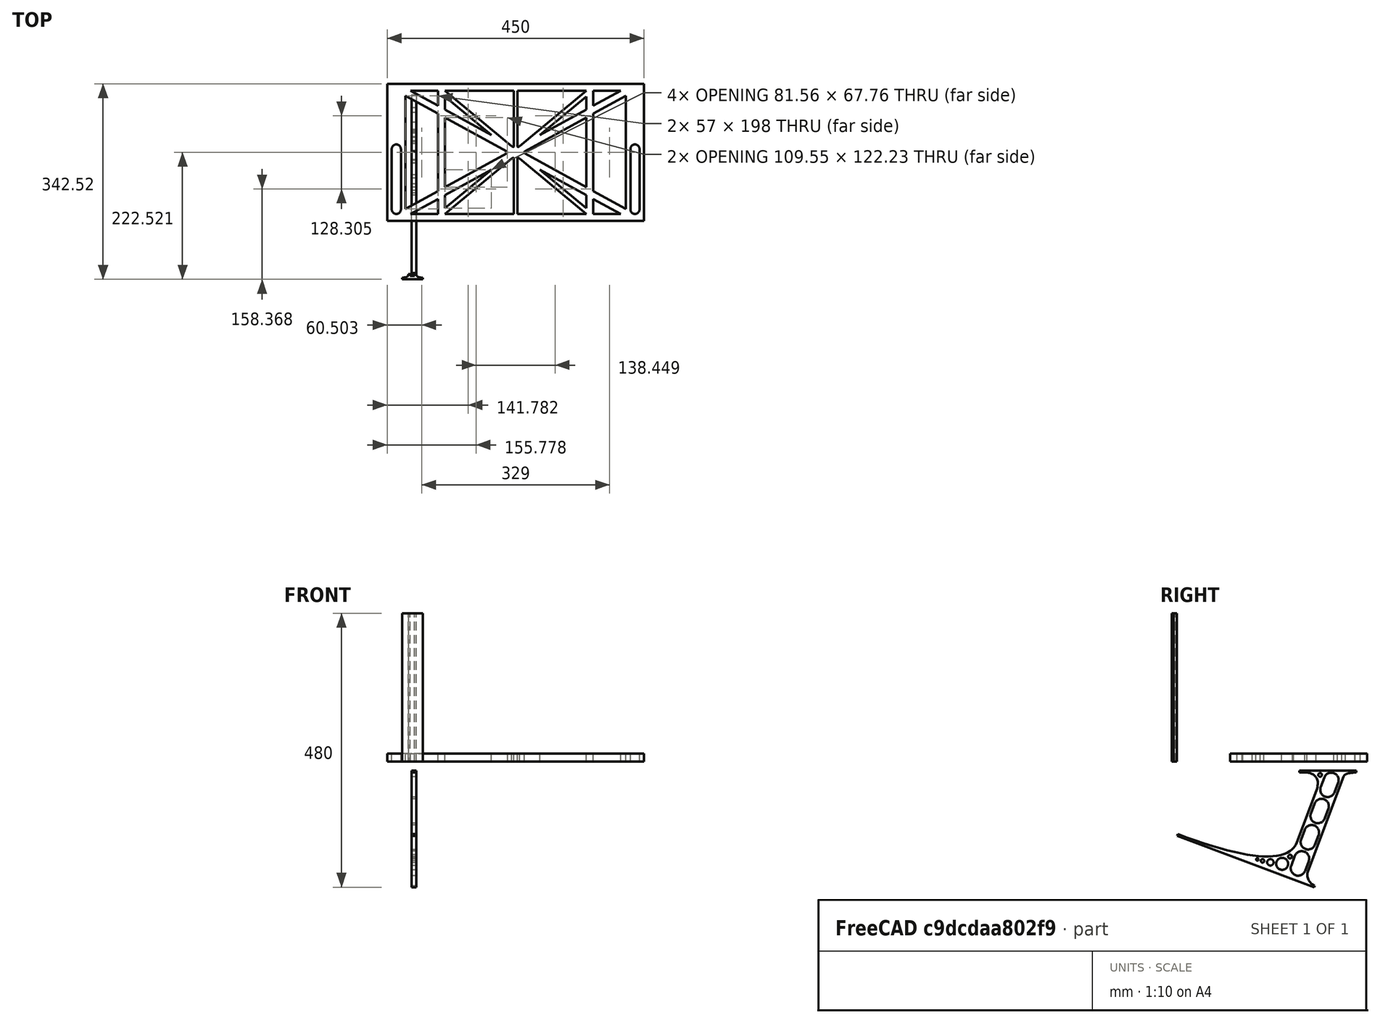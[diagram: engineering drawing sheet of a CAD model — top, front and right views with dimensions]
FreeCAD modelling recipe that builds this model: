
FCSTD DOCUMENT  (FreeCAD 0.19R0.19.2)
Label: laptopStand059
License: All rights reserved
LicenseURL: http://en.wikipedia.org/wiki/All_rights_reserved
objects: Sketcher::SketchObject×3, Part::Extrusion×3
note: 6 computed .brp shape members not serialized (recipe doc carries the construction recipe); baked Part::Feature solids carry a one-line shape summary decoded from their .brp

FEATURE [Sketcher::SketchObject] Sketch
  FullyConstrained = false
  sketch-geometry (100):
    g0: LineSegment StartX=375.073 StartY=115.221 StartZ=0 EndX=318.073 EndY=83.9235 EndZ=0
    g1: LineSegment StartX=-10.9272 StartY=-82.7794 StartZ=0 EndX=46.0728 EndY=-51.4823 EndZ=0
    g2: LineSegment StartX=-1.92718 StartY=124.221 StartZ=0 EndX=46.0728 EndY=97.8651 EndZ=0
    g3: LineSegment StartX=366.073 StartY=-91.7794 StartZ=0 EndX=318.073 EndY=-65.424 EndZ=0
    g4: LineSegment StartX=-10.9272 StartY=115.221 StartZ=0 EndX=-10.9272 EndY=-82.7794 EndZ=0
    g5: LineSegment StartX=375.073 StartY=-82.7794 StartZ=0 EndX=375.073 EndY=115.221 EndZ=0
    g6: LineSegment StartX=-1.92719 StartY=-91.7794 StartZ=0 EndX=46.0728 EndY=-91.7794 EndZ=0
    g7: LineSegment StartX=318.073 StartY=124.221 StartZ=0 EndX=366.073 EndY=124.221 EndZ=0
    g8: LineSegment StartX=306.073 StartY=-81.8102 StartZ=0 EndX=224.513 EndY=-14.0532 EndZ=0
    g9: LineSegment StartX=58.0728 StartY=114.251 StartZ=0 EndX=139.632 EndY=46.4944 EndZ=0
    g10: LineSegment StartX=306.073 StartY=124.221 StartZ=0 EndX=189.124 EndY=27.0628 EndZ=0
    g11: LineSegment StartX=58.0728 StartY=-91.7794 StartZ=0 EndX=175.022 EndY=5.37834 EndZ=0
    g12: LineSegment StartX=46.0728 StartY=124.221 StartZ=0 EndX=46.0728 EndY=97.8651 EndZ=0
    g13: LineSegment StartX=58.0728 StartY=-81.8102 StartZ=0 EndX=58.0728 EndY=-58.8351 EndZ=0
    g14: LineSegment StartX=318.073 StartY=124.221 StartZ=0 EndX=318.073 EndY=97.8651 EndZ=0
    g15: LineSegment StartX=306.073 StartY=114.251 StartZ=0 EndX=306.073 EndY=91.2763 EndZ=0
    g16: LineSegment StartX=224.513 StartY=46.4944 StartZ=0 EndX=306.073 EndY=114.251 EndZ=0
    g17: LineSegment StartX=175.022 StartY=27.0628 StartZ=0 EndX=58.0728 EndY=124.221 EndZ=0
    g18: LineSegment StartX=139.632 StartY=-14.0532 StartZ=0 EndX=58.0728 EndY=-81.8102 EndZ=0
    g19: LineSegment StartX=224.513 StartY=46.4944 StartZ=0 EndX=306.073 EndY=91.2763 EndZ=0
    g20: LineSegment StartX=139.632 StartY=-14.0532 StartZ=0 EndX=58.0728 EndY=-58.8351 EndZ=0
    g21: LineSegment StartX=189.124 StartY=5.37834 StartZ=0 EndX=306.073 EndY=-91.7794 EndZ=0
    g22: LineSegment StartX=306.073 StartY=77.3346 StartZ=0 EndX=306.073 EndY=-44.8935 EndZ=0
    g23: LineSegment StartX=318.073 StartY=83.9235 StartZ=0 EndX=318.073 EndY=-51.4823 EndZ=0
    g24: LineSegment StartX=318.073 StartY=97.8651 StartZ=0 EndX=366.073 EndY=124.221 EndZ=0
    g25: LineSegment StartX=306.073 StartY=-58.8351 StartZ=0 EndX=224.513 EndY=-14.0532 EndZ=0
    g26: LineSegment StartX=306.073 StartY=-58.8351 StartZ=0 EndX=306.073 EndY=-81.8102 EndZ=0
    g27: LineSegment StartX=318.073 StartY=-51.4823 StartZ=0 EndX=375.073 EndY=-82.7794 EndZ=0
    g28: LineSegment StartX=318.073 StartY=-65.424 StartZ=0 EndX=318.073 EndY=-91.7794 EndZ=0
    g29: LineSegment StartX=318.073 StartY=-91.7794 StartZ=0 EndX=366.073 EndY=-91.7794 EndZ=0
    g30: LineSegment StartX=58.0728 StartY=-44.8935 StartZ=0 EndX=58.0728 EndY=77.3346 EndZ=0
    g31: LineSegment StartX=46.0728 StartY=-65.424 StartZ=0 EndX=-1.92719 EndY=-91.7794 EndZ=0
    g32: LineSegment StartX=46.0728 StartY=-65.424 StartZ=0 EndX=46.0728 EndY=-91.7794 EndZ=0
    g33: LineSegment StartX=58.0728 StartY=91.2763 StartZ=0 EndX=58.0728 EndY=114.251 EndZ=0
    g34: LineSegment StartX=46.0728 StartY=83.9235 StartZ=0 EndX=46.0728 EndY=-51.4823 EndZ=0
    g35: LineSegment StartX=46.0728 StartY=124.221 StartZ=0 EndX=-1.92719 EndY=124.221 EndZ=0
    g36: LineSegment StartX=58.0728 StartY=91.2763 StartZ=0 EndX=139.632 EndY=46.4944 EndZ=0
    g37: LineSegment StartX=46.0728 StartY=83.9235 StartZ=0 EndX=-10.9272 EndY=115.221 EndZ=0
    g38: LineSegment StartX=-42.9272 StartY=136.221 StartZ=0 EndX=-42.9272 EndY=-103.779 EndZ=0
    g39: LineSegment StartX=407.073 StartY=136.221 StartZ=0 EndX=407.073 EndY=-103.779 EndZ=0
    g40: LineSegment StartX=179.022 StartY=27.0628 StartZ=0 EndX=179.022 EndY=124.221 EndZ=0
    g41: LineSegment StartX=185.124 StartY=27.0628 StartZ=0 EndX=185.124 EndY=124.221 EndZ=0
    g42: ArcOfCircle CenterX=-26.9272 CenterY=22.1087 CenterZ=0 NormalX=0 NormalY=0 NormalZ=1 AngleXU=0 Radius=8 StartAngle=1e-16 EndAngle=3.14159
    g43: ArcOfCircle CenterX=-26.9272 CenterY=-83.7794 CenterZ=0 NormalX=0 NormalY=0 NormalZ=1 AngleXU=0 Radius=8 StartAngle=3.14159 EndAngle=6.28319
    g44: LineSegment StartX=-34.9272 StartY=22.1087 StartZ=0 EndX=-34.9272 EndY=-83.7794 EndZ=0
    g45: LineSegment StartX=-18.9272 StartY=22.1087 StartZ=0 EndX=-18.9272 EndY=-83.7794 EndZ=0
    g46: LineSegment StartX=185.124 StartY=-91.7794 StartZ=0 EndX=306.073 EndY=-91.7794 EndZ=0
    g47: LineSegment StartX=179.022 StartY=-91.7794 StartZ=0 EndX=58.0728 EndY=-91.7794 EndZ=0
    g48: LineSegment StartX=306.073 StartY=124.221 StartZ=0 EndX=185.124 EndY=124.221 EndZ=0
    g49: LineSegment StartX=179.022 StartY=124.221 StartZ=0 EndX=58.0728 EndY=124.221 EndZ=0
    g50: ArcOfCircle CenterX=391.073 CenterY=22.1087 CenterZ=0 NormalX=0 NormalY=0 NormalZ=1 AngleXU=0 Radius=8 StartAngle=-4.4e-15 EndAngle=3.14159
    g51: LineSegment StartX=399.073 StartY=22.1087 StartZ=0 EndX=399.073 EndY=-83.7794 EndZ=0
    g52: LineSegment StartX=383.073 StartY=22.1087 StartZ=0 EndX=383.073 EndY=-83.7794 EndZ=0
    g53: ArcOfCircle CenterX=391.073 CenterY=-83.7794 CenterZ=0 NormalX=0 NormalY=0 NormalZ=1 AngleXU=0 Radius=8 StartAngle=3.14159 EndAngle=6.28319
    g54: Circle CenterX=175.022 CenterY=27.0628 CenterZ=0 NormalX=0 NormalY=0 NormalZ=1 AngleXU=0 Radius=1
    g55: Circle CenterX=179.022 CenterY=24.8665 CenterZ=0 NormalX=0 NormalY=0 NormalZ=1 AngleXU=0 Radius=1
    g56: Circle CenterX=179.022 CenterY=27.0628 CenterZ=0 NormalX=0 NormalY=0 NormalZ=1 AngleXU=0 Radius=1
    g57: BSplineCurve PolesCount=3 KnotsCount=2 Degree=2 IsPeriodic=0
    g58: GeomPoint X=175.022 Y=27.0628 Z=0
    g59: GeomPoint X=179.022 Y=27.0628 Z=0
    g60: Circle CenterX=189.124 CenterY=27.0628 CenterZ=0 NormalX=0 NormalY=0 NormalZ=1 AngleXU=0 Radius=1
    g61: Circle CenterX=185.124 CenterY=24.8665 CenterZ=0 NormalX=0 NormalY=0 NormalZ=1 AngleXU=0 Radius=1
    g62: Circle CenterX=185.124 CenterY=27.0628 CenterZ=0 NormalX=0 NormalY=0 NormalZ=1 AngleXU=0 Radius=1
    g63: BSplineCurve PolesCount=3 KnotsCount=2 Degree=2 IsPeriodic=0
    g64: GeomPoint X=189.124 Y=27.0628 Z=0
    g65: GeomPoint X=185.124 Y=27.0628 Z=0
    g66: Circle CenterX=175.022 CenterY=5.37834 CenterZ=0 NormalX=0 NormalY=0 NormalZ=1 AngleXU=0 Radius=1
    g67: Circle CenterX=179.022 CenterY=7.57463 CenterZ=0 NormalX=0 NormalY=0 NormalZ=1 AngleXU=0 Radius=1
    g68: Circle CenterX=179.022 CenterY=5.34704 CenterZ=0 NormalX=0 NormalY=0 NormalZ=1 AngleXU=0 Radius=1
    g69: BSplineCurve PolesCount=3 KnotsCount=2 Degree=2 IsPeriodic=0
    g70: GeomPoint X=175.022 Y=5.37834 Z=0
    g71: GeomPoint X=179.022 Y=5.34704 Z=0
    g72: Circle CenterX=189.124 CenterY=5.37834 CenterZ=0 NormalX=0 NormalY=0 NormalZ=1 AngleXU=0 Radius=1
    g73: Circle CenterX=185.124 CenterY=7.57463 CenterZ=0 NormalX=0 NormalY=0 NormalZ=1 AngleXU=0 Radius=1
    g74: Circle CenterX=185.124 CenterY=5.34704 CenterZ=0 NormalX=0 NormalY=0 NormalZ=1 AngleXU=0 Radius=1
    g75: BSplineCurve PolesCount=3 KnotsCount=2 Degree=2 IsPeriodic=0
    g76: GeomPoint X=189.124 Y=5.37834 Z=0
    g77: GeomPoint X=185.124 Y=5.34704 Z=0
    g78: LineSegment StartX=179.022 StartY=5.34704 StartZ=0 EndX=179.022 EndY=-91.7794 EndZ=0
    g79: LineSegment StartX=185.124 StartY=-91.7794 StartZ=0 EndX=185.124 EndY=5.34704 EndZ=0
    g80: Circle CenterX=165.871 CenterY=18.1458 CenterZ=0 NormalX=0 NormalY=0 NormalZ=1 AngleXU=0 Radius=1
    g81: Circle CenterX=169.377 CenterY=16.2206 CenterZ=0 NormalX=0 NormalY=0 NormalZ=1 AngleXU=0 Radius=1
    g82: Circle CenterX=165.871 CenterY=14.2954 CenterZ=0 NormalX=0 NormalY=0 NormalZ=1 AngleXU=0 Radius=1
    g83: BSplineCurve PolesCount=3 KnotsCount=2 Degree=2 IsPeriodic=0
    g84: GeomPoint X=165.871 Y=18.1458 Z=0
    g85: GeomPoint X=165.871 Y=14.2954 Z=0
    g86: Circle CenterX=198.275 CenterY=18.1458 CenterZ=0 NormalX=0 NormalY=0 NormalZ=1 AngleXU=0 Radius=1
    g87: Circle CenterX=194.768 CenterY=16.2206 CenterZ=0 NormalX=0 NormalY=0 NormalZ=1 AngleXU=0 Radius=1
    g88: Circle CenterX=198.275 CenterY=14.2954 CenterZ=0 NormalX=0 NormalY=0 NormalZ=1 AngleXU=0 Radius=1
    g89: BSplineCurve PolesCount=3 KnotsCount=2 Degree=2 IsPeriodic=0
    g90: GeomPoint X=198.275 Y=18.1458 Z=0
    g91: GeomPoint X=198.275 Y=14.2954 Z=0
    g92: LineSegment StartX=165.871 StartY=18.1458 StartZ=0 EndX=58.0728 EndY=77.3346 EndZ=0
    g93: LineSegment StartX=58.0728 StartY=-44.8935 StartZ=0 EndX=165.871 EndY=14.2954 EndZ=0
    g94: LineSegment StartX=198.275 StartY=18.1458 StartZ=0 EndX=306.073 EndY=77.3346 EndZ=0
    g95: LineSegment StartX=198.275 StartY=14.2954 StartZ=0 EndX=306.073 EndY=-44.8935 EndZ=0
    g96: LineSegment StartX=407.073 StartY=-103.779 StartZ=0 EndX=-42.9272 EndY=-103.779 EndZ=0
    g97: LineSegment StartX=407.073 StartY=136.221 StartZ=0 EndX=-42.9272 EndY=136.221 EndZ=0
    g98: LineSegment StartX=-10.9272 StartY=115.221 StartZ=0 EndX=-10.9272 EndY=140.791 EndZ=0
    g99: LineSegment StartX=-10.9272 StartY=140.791 StartZ=0 EndX=-26.9272 EndY=140.791 EndZ=0
  constraints (181):
    c: Horizontal(g6)
    c: Horizontal(g7)
    c: Coincident(g36,g9)
    c: Coincident(g16,g19)
    c: Coincident(g20,g18)
    c: Coincident(g25,g8)
    c: Coincident(g16,g15)
    c: Tangent(g15,g22)
    c: Tangent(g14,g23)
    c: Coincident(g19,g15)
    c: Tangent(g19,g24)
    c: Coincident(g0,g23)
    c: Coincident(g26,g8)
    c: Tangent(g3,g25)
    c: Tangent(g22,g26)
    c: Coincident(g23,g27)
    c: Coincident(g28,g3)
    c: Tangent(g23,g28)
    c: Coincident(g18,g13)
    c: Tangent(g13,g30)
    c: Coincident(g20,g13)
    c: Tangent(g20,g31)
    c: Coincident(g32,g31)
    c: Tangent(g12,g32)
    c: Coincident(g1,g34)
    c: Tangent(g30,g33)
    c: Tangent(g12,g34)
    c: Coincident(g9,g33)
    c: Coincident(g2,g12)
    c: Coincident(g36,g33)
    c: Tangent(g2,g36)
    c: Coincident(g37,g34)
    c: Block(g17)
    c: Block(g10)
    c: Block(g14)
    c: Block(g24)
    c: Block(g0)
    c: Block(g27)
    c: Block(g5)
    c: Block(g25)
    c: Block(g26)
    c: Block(g3)
    c: Block(g28)
    c: Block(g16)
    c: Block(g21)
    c: Block(g11)
    c: Block(g20)
    c: Block(g18)
    c: Block(g32)
    c: Block(g31)
    c: Block(g1)
    c: Block(g4)
    c: Block(g37)
    c: Block(g2)
    c: Block(g12)
    c: Block(g9)
    c: Block(g33)
    c: Block(g22)
    c: Block(g35)
    c: Block(g7)
    c: Block(g29)
    c: Block(g6)
    c: Vertical(g38)
    c: Vertical(g39)
    c: Block(g39)
    c: Block(g38)
    c: Vertical(g40)
    c: Vertical(g41)
    c: Block(g40)
    c: Block(g41)
    c: Tangent(g42,g45) = 1.5708
    c: Tangent(g42,g44) = -1.5708
    c: Tangent(g44,g43) = -1.5708
    c: Tangent(g45,g43) = 1.5708
    c: Vertical(g44)
    c: Equal(g42,g43)
    c: Block(g45)
    c: Block(g44)
    c: Coincident(g46,g21)
    c: Horizontal(g46)
    c: Coincident(g47,g11)
    c: Horizontal(g47)
    c: Coincident(g48,g10)
    c: Coincident(g48,g41)
    c: Horizontal(g48)
    c: Coincident(g49,g40)
    c: Coincident(g49,g17)
    c: Horizontal(g49)
    c: Tangent(g50,g51) = 1.5708
    c: Tangent(g51,g53) = 1.5708
    c: Equal(g50,g53)
    c: Coincident(g52,g50)
    c: Coincident(g52,g53)
    c: Block(g51)
    c: Block(g52)
    c: Coincident(g57,g17)
    c: Weight(g54) = 1
    c: Equal(g54,g55)
    c: Equal(g54,g56)
    c: Coincident(g57,g40)
    c: InternalAlignment(g54,g57)
    c: InternalAlignment(g55,g57)
    c: InternalAlignment(g56,g57)
    c: InternalAlignment(g58,g57)
    c: InternalAlignment(g59,g57)
    c: Coincident(g63,g10)
    c: Weight(g60) = 1
    c: Equal(g60,g61)
    c: Equal(g60,g62)
    c: Coincident(g63,g41)
    c: InternalAlignment(g60,g63)
    c: InternalAlignment(g61,g63)
    c: InternalAlignment(g62,g63)
    c: InternalAlignment(g64,g63)
    c: InternalAlignment(g65,g63)
    c: Block(g63)
    c: Block(g57)
    c: Coincident(g69,g11)
    c: Weight(g66) = 1
    c: Equal(g66,g67)
    c: Equal(g66,g68)
    c: InternalAlignment(g66,g69)
    c: InternalAlignment(g67,g69)
    c: InternalAlignment(g68,g69)
    c: InternalAlignment(g70,g69)
    c: InternalAlignment(g71,g69)
    c: Weight(g72) = 1
    c: Equal(g72,g73)
    c: Equal(g72,g74)
    c: InternalAlignment(g72,g75)
    c: InternalAlignment(g73,g75)
    c: InternalAlignment(g74,g75)
    c: InternalAlignment(g76,g75)
    c: InternalAlignment(g77,g75)
    c: Block(g75)
    c: Block(g69)
    c: Coincident(g78,g69)
    c: Coincident(g78,g47)
    c: Vertical(g78)
    c: Coincident(g79,g46)
    c: Coincident(g79,g75)
    c: Vertical(g79)
    c: Weight(g80) = 1
    c: Equal(g80,g81)
    c: Equal(g80,g82)
    c: InternalAlignment(g80,g83)
    c: InternalAlignment(g81,g83)
    c: InternalAlignment(g82,g83)
    c: InternalAlignment(g84,g83)
    c: InternalAlignment(g85,g83)
    c: Weight(g86) = 1
    c: Equal(g86,g87)
    c: Equal(g86,g88)
    c: InternalAlignment(g86,g89)
    c: InternalAlignment(g87,g89)
    c: InternalAlignment(g88,g89)
    c: InternalAlignment(g90,g89)
    c: InternalAlignment(g91,g89)
    c: Block(g83)
    c: Block(g89)
    c: Coincident(g92,g83)
    c: Coincident(g92,g30)
    c: Coincident(g93,g30)
    c: Coincident(g93,g83)
    c: Coincident(g94,g89)
    c: Coincident(g94,g22)
    c: Coincident(g95,g89)
    c: Coincident(g95,g22)
    c: Block(g30)
    c: Coincident(g96,g39)
    c: Coincident(g96,g38)
    c: Horizontal(g96)
    c: Distance(g96) = 450
    c: Coincident(g97,g39)
    c: Coincident(g97,g38)
    c: Horizontal(g97)
    c: Coincident(g98,g4)
    c: Vertical(g98)
    c: Coincident(g99,g98)
    c: Horizontal(g99)
    c: Distance(g99) = 16
FEATURE [Sketcher::SketchObject] Sketch001
  FullyConstrained = true
  MapMode = 4
  Placement = pos=(0,0,0) rot=(0.57735,0.57735,0.57735;2.0944rad)
  Support = -> [Sketch]
  sketch-geometry (46):
    g0: BSplineCurve PolesCount=3 KnotsCount=2 Degree=2 IsPeriodic=0
    g1: ArcOfCircle CenterX=73.1223 CenterY=-32.291 CenterZ=0 NormalX=0 NormalY=0 NormalZ=1 AngleXU=0 Radius=13 StartAngle=5.92268 EndAngle=9.06428
    g2: ArcOfCircle CenterX=66.7816 CenterY=-49.1439 CenterZ=0 NormalX=0 NormalY=0 NormalZ=1 AngleXU=0 Radius=13 StartAngle=2.78068 EndAngle=5.92131
    g3: ArcOfCircle CenterX=55.9263 CenterY=-78.1807 CenterZ=0 NormalX=0 NormalY=0 NormalZ=1 AngleXU=0 Radius=13 StartAngle=5.92268 EndAngle=9.06428
    g4: ArcOfCircle CenterX=49.5884 CenterY=-95.0342 CenterZ=0 NormalX=0 NormalY=0 NormalZ=1 AngleXU=0 Radius=13 StartAngle=2.78068 EndAngle=5.92131
    g5: ArcOfCircle CenterX=38.7206 CenterY=-124.067 CenterZ=0 NormalX=0 NormalY=0 NormalZ=1 AngleXU=0 Radius=13 StartAngle=5.92268 EndAngle=9.06428
    g6: ArcOfCircle CenterX=32.3875 CenterY=-140.92 CenterZ=0 NormalX=0 NormalY=0 NormalZ=1 AngleXU=0 Radius=13 StartAngle=2.78068 EndAngle=5.92131
    g7: ArcOfCircle CenterX=21.4715 CenterY=-169.934 CenterZ=0 NormalX=0 NormalY=0 NormalZ=1 AngleXU=0 Radius=13 StartAngle=5.92268 EndAngle=9.06428
    g8: ArcOfCircle CenterX=15.1336 CenterY=-186.787 CenterZ=0 NormalX=0 NormalY=0 NormalZ=1 AngleXU=0 Radius=13 StartAngle=2.78068 EndAngle=5.92131
    g9-g12: Circle x4 (B-spline internal-alignment scaffolding for g13; pole/knot coordinates omitted)
    g13: BSplineCurve PolesCount=4 KnotsCount=2 Degree=3 IsPeriodic=0
    g14: GeomPoint X=28.8094 Y=-19.0875 Z=0
    g15: GeomPoint X=47.0443 Y=-50.4712 Z=0
    g16: Circle CenterX=53.5586 CenterY=-23.2695 CenterZ=0 NormalX=0 NormalY=0 NormalZ=1 AngleXU=0 Radius=3.24518
    g17: Circle CenterX=-195.441 CenterY=-127.082 CenterZ=0 NormalX=0 NormalY=0 NormalZ=1 AngleXU=0 Radius=1
    g18: Circle CenterX=-8.24091 CenterY=-197.481 CenterZ=0 NormalX=0 NormalY=0 NormalZ=1 AngleXU=0 Radius=1
    g19: Circle CenterX=12.8789 CenterY=-141.321 CenterZ=0 NormalX=0 NormalY=0 NormalZ=1 AngleXU=0 Radius=1
    g20: BSplineCurve PolesCount=3 KnotsCount=2 Degree=2 IsPeriodic=0
    g21: GeomPoint X=-195.441 Y=-127.082 Z=0
    g22: GeomPoint X=12.8789 Y=-141.321 Z=0
    g23: Circle CenterX=-12.8016 CenterY=-179.036 CenterZ=0 NormalX=0 NormalY=0 NormalZ=1 AngleXU=0 Radius=10.5072
    g24: Circle CenterX=0.933922 CenterY=-166.43 CenterZ=0 NormalX=0 NormalY=0 NormalZ=1 AngleXU=0 Radius=3.26661
    g25: Circle CenterX=-33.5518 CenterY=-176.44 CenterZ=0 NormalX=0 NormalY=0 NormalZ=1 AngleXU=0 Radius=5.64388
    g26: Circle CenterX=-47.2366 CenterY=-173.859 CenterZ=0 NormalX=0 NormalY=0 NormalZ=1 AngleXU=0 Radius=3.01653
    g27: Circle CenterX=-56.2595 CenterY=-171.456 CenterZ=0 NormalX=0 NormalY=0 NormalZ=1 AngleXU=0 Radius=2.12826
    g28: ArcOfCircle CenterX=51.2151 CenterY=-198.473 CenterZ=0 NormalX=0 NormalY=0 NormalZ=1 AngleXU=0 Radius=20 StartAngle=2.78189 EndAngle=4.35269
    g29: LineSegment StartX=32.4951 StartY=-191.433 StartZ=0 EndX=94.6578 EndY=-26.1352 EndZ=0
    g30: LineSegment StartX=43.1192 StartY=-220.001 StartZ=0 EndX=-196.497 EndY=-129.89 EndZ=0
    g31: LineSegment StartX=43.1192 StartY=-220.001 StartZ=0 EndX=44.1752 EndY=-217.193 EndZ=0
    g32: LineSegment StartX=117.223 StartY=-19.0875 StartZ=0 EndX=117.223 EndY=-16.0875 EndZ=0
    g33: LineSegment StartX=117.223 StartY=-16.0875 StartZ=0 EndX=17.2232 EndY=-16.0875 EndZ=0
    g34: LineSegment StartX=17.2232 StartY=-16.0875 StartZ=0 EndX=17.2232 EndY=-19.0875 EndZ=0
    g35: LineSegment StartX=28.8094 StartY=-19.0875 StartZ=0 EndX=17.2232 EndY=-19.0875 EndZ=0
    g36: LineSegment StartX=47.0443 StartY=-50.4712 StartZ=0 EndX=12.8789 EndY=-141.321 EndZ=0
    g37: LineSegment StartX=-195.441 StartY=-127.082 StartZ=0 EndX=-196.497 EndY=-129.89 EndZ=0
    g38: LineSegment StartX=85.2866 StartY=-36.8766 StartZ=0 EndX=78.9396 EndY=-53.7463 EndZ=0
    g39: LineSegment StartX=60.9579 StartY=-27.7053 StartZ=0 EndX=54.6191 EndY=-44.5532 EndZ=0
    g40: LineSegment StartX=68.0907 StartY=-82.7664 StartZ=0 EndX=61.7465 EndY=-99.6365 EndZ=0
    g41: LineSegment StartX=43.7619 StartY=-73.595 StartZ=0 EndX=37.426 EndY=-90.4435 EndZ=0
    g42: LineSegment StartX=50.885 StartY=-128.652 StartZ=0 EndX=44.5456 EndY=-145.522 EndZ=0
    g43: LineSegment StartX=26.5562 StartY=-119.481 StartZ=0 EndX=20.2251 EndY=-136.329 EndZ=0
    g44: LineSegment StartX=9.3071 StartY=-165.349 StartZ=0 EndX=2.97115 EndY=-182.197 EndZ=0
    g45: LineSegment StartX=33.6358 StartY=-174.52 StartZ=0 EndX=27.2917 EndY=-191.39 EndZ=0
  constraints (71):
    c: Block(g0)
    c: Block(g1)
    c: Block(g2)
    c: Block(g4)
    c: Block(g3)
    c: Block(g6)
    c: Block(g5)
    c: Block(g8)
    c: Block(g7)
    c: Weight(g9) = 1
    c: Equal(g9,g10)
    c: Equal(g9,g11)
    c: Equal(g9,g12)
    c: InternalAlignment(g9-g12 -> g13) x4
    c: InternalAlignment(g14,g13)
    c: InternalAlignment(g15,g13)
    c: Block(g16)
    c: Weight(g17) = 1
    c: Equal(g17,g18)
    c: Equal(g17,g19)
    c: InternalAlignment(g17,g20)
    c: InternalAlignment(g18,g20)
    c: InternalAlignment(g19,g20)
    c: InternalAlignment(g21,g20)
    c: InternalAlignment(g22,g20)
    c: Block(g20)
    c: Block(g23)
    c: Block(g24)
    c: Block(g25)
    c: Block(g26)
    c: Block(g27)
    c: Block(g28)
    c: Coincident(g29,g28)
    c: Coincident(g29,g0)
    c: Block(g13)
    c: Coincident(g31,g30)
    c: Coincident(g31,g28)
    c: Block(g31)
    c: Coincident(g32,g0)
    c: Vertical(g32)
    c: Coincident(g33,g32)
    c: Horizontal(g33)
    c: Coincident(g34,g33)
    c: Vertical(g34)
    c: Block(g33)
    c: Coincident(g35,g13)
    c: Coincident(g35,g34)
    c: Horizontal(g35)
    c: Coincident(g36,g13)
    c: Coincident(g36,g20)
    c: Coincident(g37,g20)
    c: Coincident(g37,g30)
    c: Block(g30)
    c: Coincident(g38,g1)
    c: Coincident(g38,g2)
    c: Coincident(g39,g1)
    c: Coincident(g39,g2)
    c: Coincident(g40,g3)
    c: Coincident(g40,g4)
    c: Coincident(g41,g3)
    c: Coincident(g41,g4)
    c: Coincident(g42,g5)
    c: Coincident(g42,g6)
    c: Coincident(g43,g5)
    c: Coincident(g43,g6)
    c: Coincident(g44,g7)
    c: Coincident(g44,g8)
    c: Coincident(g45,g7)
    c: Coincident(g45,g8)
    c: Distance(g30) = 256
    c: Distance(g33) = 100
FEATURE [Part::Extrusion] Extrude002
  Base = -> Sketch001
  Dir = (1,0,0)
  DirMode = 2
  FaceMakerClass = Part::FaceMakerBullseye
  LengthFwd = 8
  LengthRev = 0
  Solid = true
  Symmetric = false
FEATURE [Sketcher::SketchObject] Sketch002
  FullyConstrained = true
  sketch-geometry (20):
    g0: LineSegment StartX=-2.77179 StartY=-200.304 StartZ=0 EndX=5.22821 EndY=-200.304 EndZ=0
    g1: LineSegment StartX=5.22821 StartY=-200.304 StartZ=0 EndX=5.22821 EndY=-197.304 EndZ=0
    g2: LineSegment StartX=-2.77179 StartY=-200.304 StartZ=0 EndX=-2.77179 EndY=-197.304 EndZ=0
    g3: LineSegment StartX=5.22821 StartY=-197.304 StartZ=0 EndX=8.22821 EndY=-197.304 EndZ=0
    g4: LineSegment StartX=-2.77179 StartY=-197.304 StartZ=0 EndX=-5.77179 EndY=-197.304 EndZ=0
    g5: LineSegment StartX=19.2282 StartY=-203.304 StartZ=0 EndX=19.2282 EndY=-206.304 EndZ=0
    g6: LineSegment StartX=-16.7718 StartY=-203.304 StartZ=0 EndX=-16.7718 EndY=-206.304 EndZ=0
    g7: LineSegment StartX=-16.7718 StartY=-206.304 StartZ=0 EndX=19.2282 EndY=-206.304 EndZ=0
    g8: Circle CenterX=-16.7718 CenterY=-203.304 CenterZ=0 NormalX=0 NormalY=0 NormalZ=1 AngleXU=0 Radius=1
    g9: Circle CenterX=-5.77179 CenterY=-203.304 CenterZ=0 NormalX=0 NormalY=0 NormalZ=1 AngleXU=0 Radius=1
    g10: Circle CenterX=-5.77179 CenterY=-197.304 CenterZ=0 NormalX=0 NormalY=0 NormalZ=1 AngleXU=0 Radius=1
    g11: BSplineCurve PolesCount=3 KnotsCount=2 Degree=2 IsPeriodic=0
    g12: GeomPoint X=-16.7718 Y=-203.304 Z=0
    g13: GeomPoint X=-5.77179 Y=-197.304 Z=0
    g14: Circle CenterX=19.2282 CenterY=-203.304 CenterZ=0 NormalX=0 NormalY=0 NormalZ=1 AngleXU=0 Radius=1
    g15: Circle CenterX=8.22821 CenterY=-203.304 CenterZ=0 NormalX=0 NormalY=0 NormalZ=1 AngleXU=0 Radius=1
    g16: Circle CenterX=8.22821 CenterY=-197.304 CenterZ=0 NormalX=0 NormalY=0 NormalZ=1 AngleXU=0 Radius=1
    g17: BSplineCurve PolesCount=3 KnotsCount=2 Degree=2 IsPeriodic=0
    g18: GeomPoint X=19.2282 Y=-203.304 Z=0
    g19: GeomPoint X=8.22821 Y=-197.304 Z=0
  constraints (41):
    c: Horizontal(g0)
    c: Distance(g0) = 8
    c: Coincident(g1,g0)
    c: Vertical(g1)
    c: Distance(g1) = 3
    c: Coincident(g2,g0)
    c: Vertical(g2)
    c: Distance(g2) = 3
    c: Coincident(g3,g1)
    c: Horizontal(g3)
    c: Distance(g3) = 3
    c: Coincident(g4,g2)
    c: Horizontal(g4)
    c: Distance(g4) = 3
    c: Vertical(g5)
    c: Vertical(g6)
    c: Coincident(g7,g6)
    c: Coincident(g7,g5)
    c: Weight(g8) = 1
    c: Equal(g8,g9)
    c: Equal(g8,g10)
    c: Coincident(g11,g4)
    c: InternalAlignment(g8,g11)
    c: InternalAlignment(g9,g11)
    c: InternalAlignment(g10,g11)
    c: InternalAlignment(g12,g11)
    c: InternalAlignment(g13,g11)
    c: Coincident(g17,g5)
    c: Weight(g14) = 1
    c: Equal(g14,g15)
    c: Equal(g14,g16)
    c: Coincident(g17,g3)
    c: InternalAlignment(g14,g17)
    c: InternalAlignment(g15,g17)
    c: InternalAlignment(g16,g17)
    c: InternalAlignment(g18,g17)
    c: InternalAlignment(g19,g17)
    c: Block(g7)
    c: Block(g17)
    c: Block(g11)
    c: Block(g6)
FEATURE [Part::Extrusion] Extrude003
  Base = -> Sketch002
  Dir = (0,0,1)
  DirMode = 2
  FaceMakerClass = Part::FaceMakerBullseye
  LengthFwd = 260
  LengthRev = 0
  Solid = true
  Symmetric = false
FEATURE [Part::Extrusion] Extrude
  Base = -> Sketch
  Dir = (0,0,1)
  DirMode = 2
  FaceMakerClass = Part::FaceMakerBullseye
  LengthFwd = 14
  LengthRev = 0
  Solid = true
  Symmetric = false
